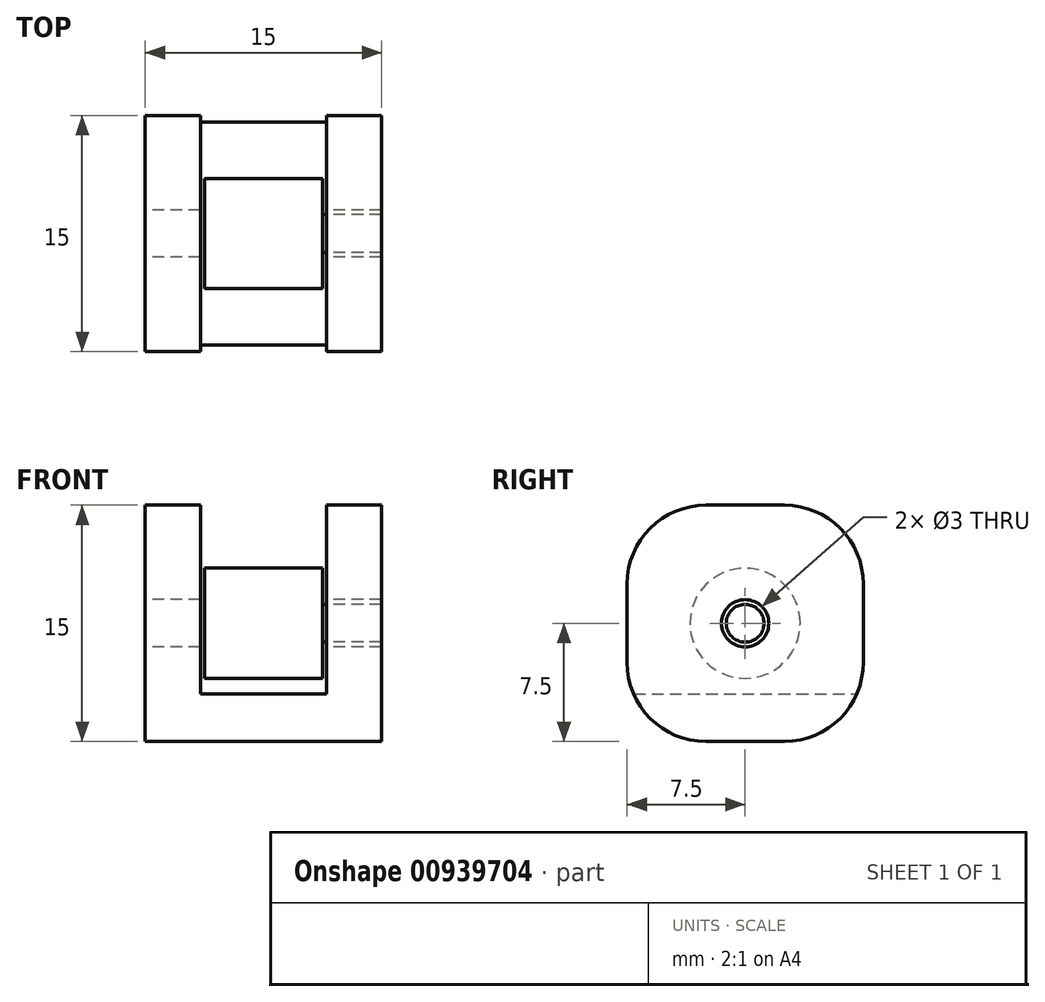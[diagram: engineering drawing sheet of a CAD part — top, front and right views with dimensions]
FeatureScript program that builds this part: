
annotation { "Feature Type Name" : "Feature", "Feature Type Description" : "" }
export const myFeature = defineFeature(function(context is Context, id is Id, definition is map)
    precondition{}
    {
        {
            var Q0;
            Q0=qCreatedBy(makeId("Top.planeOp"),FACE);
            var sketch = newSketch(context, id + "F0", { "sketchPlane" : qUnion([Q0])});
            skLineSegment(sketch, "E0.bottom", {"start": v(7.5, 7.5) * mm, "end": v(-7.5, 7.5) * mm});
            skLineSegment(sketch, "E0.top", {"start": v(7.5, -7.5) * mm, "end": v(-7.5, -7.5) * mm});
            skLineSegment(sketch, "E0.left", {"start": v(7.5, 7.5) * mm, "end": v(7.5, -7.5) * mm});
            skLineSegment(sketch, "E0.right", {"start": v(-7.5, 7.5) * mm, "end": v(-7.5, -7.5) * mm});
            skPoint(sketch, "E0.middle", {"position": v(0, 0) * mm});
            skSolve(sketch);
        }
        {
            var Q0;
            Q0 = qSketchRegion(id + "F0", true);
            extrude(context, id + "F1", {"entities" : qUnion([Q0]), "depth" : 15 * mm, "offsetDistance" : 25 * mm});
        }
        {
            var Q0;
            Q0=makeQuery(id+"F1.opExtrude","SWEPT_FACE",FACE,{"disambiguationData":[OSD([sQuery(id+"F0.wireOp",EDGE,"E0.right")])]});
            var sketch = newSketch(context, id + "F2", { "sketchPlane" : qUnion([Q0])});
            skPoint(sketch, "E1", {"position": v(0, 7.5) * mm});
            skPoint(sketch, "E1.positionSnap0", {"position": v(-7.5, 7.5) * mm});
            skPoint(sketch, "E1.positionSnap1", {"position": v(0, 15) * mm});
            skSolve(sketch);
        }
        {
            var Q0;
            Q0=sQuery(id+"F2.wireOp",VERTEX,"E1");
            var Q1;
            Q1=makeQuery(id+"F1.opExtrude","SWEPT_BODY",BODY,{"disambiguationData":[OSD([sQuery(id+"F0.wireOp",EDGE,"E0.bottom"),sQuery(id+"F0.wireOp",EDGE,"E0.top"),sQuery(id+"F0.wireOp",EDGE,"E0.left"),sQuery(id+"F0.wireOp",EDGE,"E0.right")])]});
            hole(context, id + "F3", {"style" : HoleStyle.SIMPLE, "endStyle" : HoleEndStyle.THROUGH, "holeDiameter" : 3 * mm, "majorDiameter" : 5 * mm, "isTappedThrough" : true, "tappedDepth" : 12 * mm, "tapClearance" : 3, "locations" : qUnion([Q0]), "scope" : qUnion([Q1])});
        }
        {
            var Q0;
            Q0=makeQuery(id+"F1.opExtrude","SWEPT_FACE",FACE,{"disambiguationData":[OSD([sQuery(id+"F0.wireOp",EDGE,"E0.bottom")])]});
            var sketch = newSketch(context, id + "F4", { "sketchPlane" : qUnion([Q0])});
            skLineSegment(sketch, "E2.bottom", {"start": v(-4, 15) * mm, "end": v(4, 15) * mm});
            skLineSegment(sketch, "E2.top", {"start": v(-4, 3) * mm, "end": v(4, 3) * mm});
            skLineSegment(sketch, "E2.left", {"start": v(-4, 15) * mm, "end": v(-4, 3) * mm});
            skLineSegment(sketch, "E2.right", {"start": v(4, 15) * mm, "end": v(4, 3) * mm});
            skSolve(sketch);
        }
        {
            var Q0;
            Q0 = qSketchRegion(id + "F4", true);
            extrude(context, id + "F5", {"entities" : qUnion([Q0]), "operationType" : NewBodyOperationType.REMOVE, "endBound" : BoundingType.THROUGH_ALL, "oppositeDirection" : true, "depth" : 25 * mm, "offsetDistance" : 25 * mm});
        }
        {
            var Q0;
            Q0=qCreatedBy(makeId("Right.planeOp"),FACE);
            var sketch = newSketch(context, id + "F6", { "sketchPlane" : qUnion([Q0])});
            skCircle(sketch, "E3", {"center": v(0, 7.5) * mm, "radius": 3.5 * mm});
            skSolve(sketch);
        }
        {
            var Q0;
            Q0 = qSketchRegion(id + "F6", true);
            extrude(context, id + "F7", {"entities" : qUnion([Q0]), "endBound" : BoundingType.SYMMETRIC, "depth" : 7.5 * mm, "offsetDistance" : 25 * mm});
        }
        {
            var Q0;
            Q0=makeQuery(id+"F7.opExtrude","CAP_FACE",FACE,{"disambiguationData":[OSD([sQuery(id+"F6.wireOp",EDGE,"E3")])],"isStart":false});
            var sketch = newSketch(context, id + "F8", { "sketchPlane" : qUnion([Q0])});
            skCircle(sketch, "E4", {"center": v(0, 7.5) * mm, "radius": 1.2 * mm});
            skSolve(sketch);
        }
        {
            var Q0;
            Q0 = qSketchRegion(id + "F8", true);
            var Q1;
            Q1=makeQuery(id+"F1.opExtrude","SWEPT_FACE",FACE,{"disambiguationData":[OSD([sQuery(id+"F0.wireOp",EDGE,"E0.left")])]});
            extrude(context, id + "F9", {"entities" : qUnion([Q0]), "operationType" : NewBodyOperationType.ADD, "depth" : 3.75 * mm, "endBoundEntityFace" : qUnion([Q1]), "offsetDistance" : 25 * mm});
        }
        {
            var Q0;
            {var subQ0=sQuery(id+"F0.wireOp",EDGE,"E0.right");var subQ1=sQuery(id+"F0.wireOp",EDGE,"E0.top");Q0=makeQuery(id+"F5.boolean.opBoolean","SPLIT",EDGE,{"disambiguationData":[TD([makeQuery(id+"F1.opExtrude","SWEPT_FACE",FACE,{"disambiguationData":[OSD([subQ0])]})])],"derivedFrom":makeQuery(id+"F1.opExtrude","CAP_EDGE",EDGE,{"disambiguationData":[OSD([subQ1])],"isStart":false})});}
            var Q1;
            {var subQ0=sQuery(id+"F0.wireOp",EDGE,"E0.left");var subQ1=sQuery(id+"F0.wireOp",EDGE,"E0.top");Q1=makeQuery(id+"F5.boolean.opBoolean","SPLIT",EDGE,{"disambiguationData":[TD([makeQuery(id+"F1.opExtrude","SWEPT_FACE",FACE,{"disambiguationData":[OSD([subQ0])]})])],"derivedFrom":makeQuery(id+"F1.opExtrude","CAP_EDGE",EDGE,{"disambiguationData":[OSD([subQ1])],"isStart":false})});}
            var Q2;
            {var subQ0=sQuery(id+"F0.wireOp",EDGE,"E0.bottom");var subQ1=sQuery(id+"F0.wireOp",EDGE,"E0.right");Q2=makeQuery(id+"F5.boolean.opBoolean","SPLIT",EDGE,{"disambiguationData":[TD([makeQuery(id+"F1.opExtrude","SWEPT_FACE",FACE,{"disambiguationData":[OSD([subQ1])]})])],"derivedFrom":makeQuery(id+"F1.opExtrude","CAP_EDGE",EDGE,{"disambiguationData":[OSD([subQ0])],"isStart":false})});}
            var Q3;
            {var subQ0=sQuery(id+"F0.wireOp",EDGE,"E0.bottom");var subQ1=sQuery(id+"F0.wireOp",EDGE,"E0.left");Q3=makeQuery(id+"F5.boolean.opBoolean","SPLIT",EDGE,{"disambiguationData":[TD([makeQuery(id+"F1.opExtrude","SWEPT_FACE",FACE,{"disambiguationData":[OSD([subQ1])]})])],"derivedFrom":makeQuery(id+"F1.opExtrude","CAP_EDGE",EDGE,{"disambiguationData":[OSD([subQ0])],"isStart":false})});}
            var Q4;
            Q4=makeQuery(id+"F1.opExtrude","CAP_EDGE",EDGE,{"disambiguationData":[OSD([sQuery(id+"F0.wireOp",EDGE,"E0.bottom")])],"isStart":true});
            var Q5;
            Q5=makeQuery(id+"F1.opExtrude","CAP_EDGE",EDGE,{"disambiguationData":[OSD([sQuery(id+"F0.wireOp",EDGE,"E0.top")])],"isStart":true});
            fillet(context, id + "F10", {"entities" : qUnion([Q0, Q1, Q2, Q3, Q4, Q5]), "radius" : 5 * mm, "tangentPropagation" : true, "allowEdgeOverflow" : false});
        }
    });
